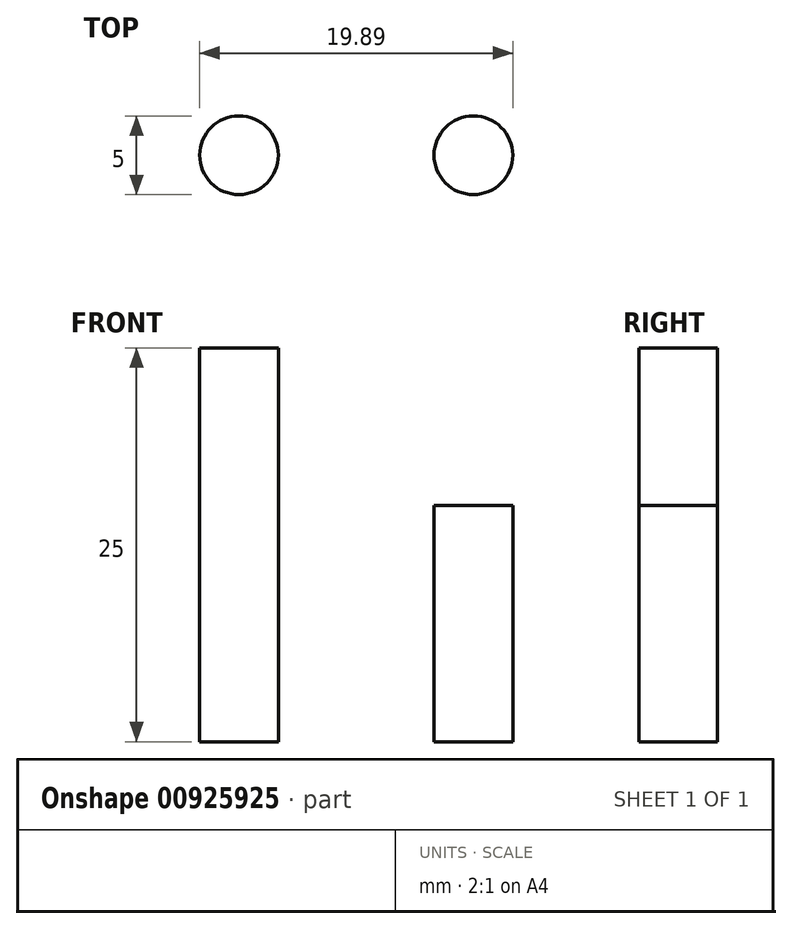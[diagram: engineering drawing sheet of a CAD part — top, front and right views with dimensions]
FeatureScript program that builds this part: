
annotation { "Feature Type Name" : "Feature", "Feature Type Description" : "" }
export const myFeature = defineFeature(function(context is Context, id is Id, definition is map)
    precondition{}
    {
        {
            var Q0;
            Q0=qCreatedBy(makeId("Top.planeOp"),FACE);
            var sketch = newSketch(context, id + "F0", { "sketchPlane" : qUnion([Q0])});
            skCircle(sketch, "E0", {"center": v(0, 0) * mm, "radius": 2.5 * mm});
            skSolve(sketch);
        }
        {
            var Q0;
            Q0=qSketchRegion(id+"F0",true);
            extrude(context, id + "F1", {"entities" : qUnion([Q0]), "depth" : 25 * mm, "offsetDistance" : 25 * mm});
        }
        {
            var Q0;
            Q0=qCreatedBy(makeId("Top.planeOp"),FACE);
            var sketch = newSketch(context, id + "F2", { "sketchPlane" : qUnion([Q0])});
            skCircle(sketch, "E1", {"center": v(14.89, 0) * mm, "radius": 2.5 * mm});
            skSolve(sketch);
        }
        {
            var Q0;
            Q0 = qSketchRegion(id + "F2", true);
            extrude(context, id + "F3", {"entities" : qUnion([Q0]), "depth" : 15 * mm, "offsetDistance" : 25 * mm});
        }
    });
